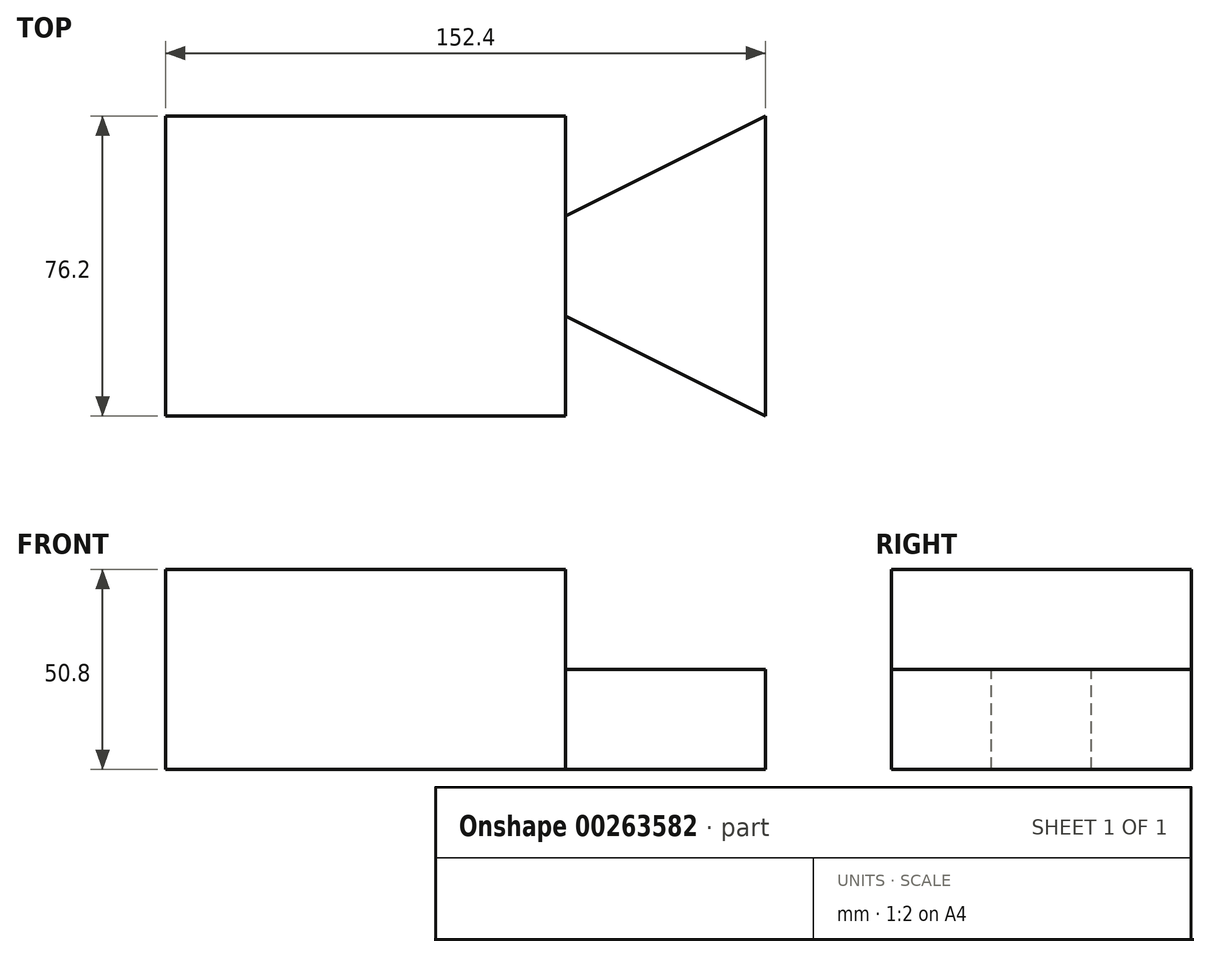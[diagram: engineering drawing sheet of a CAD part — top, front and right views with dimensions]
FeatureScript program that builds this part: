
annotation { "Feature Type Name" : "Feature", "Feature Type Description" : "" }
export const myFeature = defineFeature(function(context is Context, id is Id, definition is map)
    precondition{}
    {
        {
            var Q0;
            Q0=qCreatedBy(makeId("Front.planeOp"),FACE);
            var sketch = newSketch(context, id + "F0", { "sketchPlane" : qUnion([Q0])});
            skLineSegment(sketch, "E0.bottom", {"start": v(0, 0) * mm, "end": v(101.6, 0) * mm});
            skLineSegment(sketch, "E0.top", {"start": v(0, 50.8) * mm, "end": v(101.6, 50.8) * mm});
            skLineSegment(sketch, "E0.left", {"start": v(0, 0) * mm, "end": v(0, 50.8) * mm});
            skLineSegment(sketch, "E0.right", {"start": v(101.6, 0) * mm, "end": v(101.6, 50.8) * mm});
            skLineSegment(sketch, "E1", {"start": v(101.6, 0) * mm, "end": v(152.4, 0) * mm});
            skLineSegment(sketch, "E2", {"start": v(152.4, 0) * mm, "end": v(152.4, 25.4) * mm});
            skLineSegment(sketch, "E3", {"start": v(152.4, 25.4) * mm, "end": v(101.6, 25.4) * mm});
            skSolve(sketch);
        }
        {
            var Q0;
            {var subQ1=sQuery(id+"F0.wireOp",EDGE,"E0.bottom");Q0=makeQuery(id+"F0.imprint","IMPRINT",FACE,{"disambiguationData":[TD([[makeQuery(id+"F0.imprint","IMPRINT",EDGE,{"derivedFrom":subQ1}),1.0]])]});}
            extrude(context, id + "F1", {"entities" : qUnion([Q0]), "depth" : 76.2 * mm});
        }
        {
            var Q0;
            {var subQ0=sQuery(id+"F0.wireOp",EDGE,"E1");Q0=makeQuery(id+"F0.imprint","IMPRINT",FACE,{"disambiguationData":[TD([[makeQuery(id+"F0.imprint","IMPRINT",EDGE,{"derivedFrom":subQ0}),1.0]])]});}
            extrude(context, id + "F2", {"entities" : qUnion([Q0]), "operationType" : NewBodyOperationType.ADD, "depth" : 76.2 * mm});
        }
        {
            var Q0;
            Q0=makeQuery(id+"F2.opExtrude","SWEPT_FACE",FACE,{"disambiguationData":[OSD([sQuery(id+"F0.wireOp",EDGE,"E3")])]});
            var sketch = newSketch(context, id + "F3", { "sketchPlane" : qUnion([Q0])});
            skLineSegment(sketch, "E4", {"start": v(101.6, -76.2) * mm, "end": v(101.6, -50.8) * mm});
            skLineSegment(sketch, "E5", {"start": v(101.6, -50.8) * mm, "end": v(152.4, -76.2) * mm});
            skLineSegment(sketch, "E6", {"start": v(152.4, -76.2) * mm, "end": v(101.6, -76.2) * mm});
            skLineSegment(sketch, "E7", {"start": v(101.6, 0) * mm, "end": v(101.6, -25.4) * mm});
            skLineSegment(sketch, "E8", {"start": v(101.6, -25.4) * mm, "end": v(152.4, 0) * mm});
            skLineSegment(sketch, "E9", {"start": v(152.4, 0) * mm, "end": v(101.6, 0) * mm});
            skSolve(sketch);
        }
        {
            var Q0;
            Q0 = qSketchRegion(id + "F3", true);
            extrude(context, id + "F4", {"entities" : qUnion([Q0]), "operationType" : NewBodyOperationType.REMOVE, "oppositeDirection" : true, "depth" : 25.4 * mm});
        }
    });
